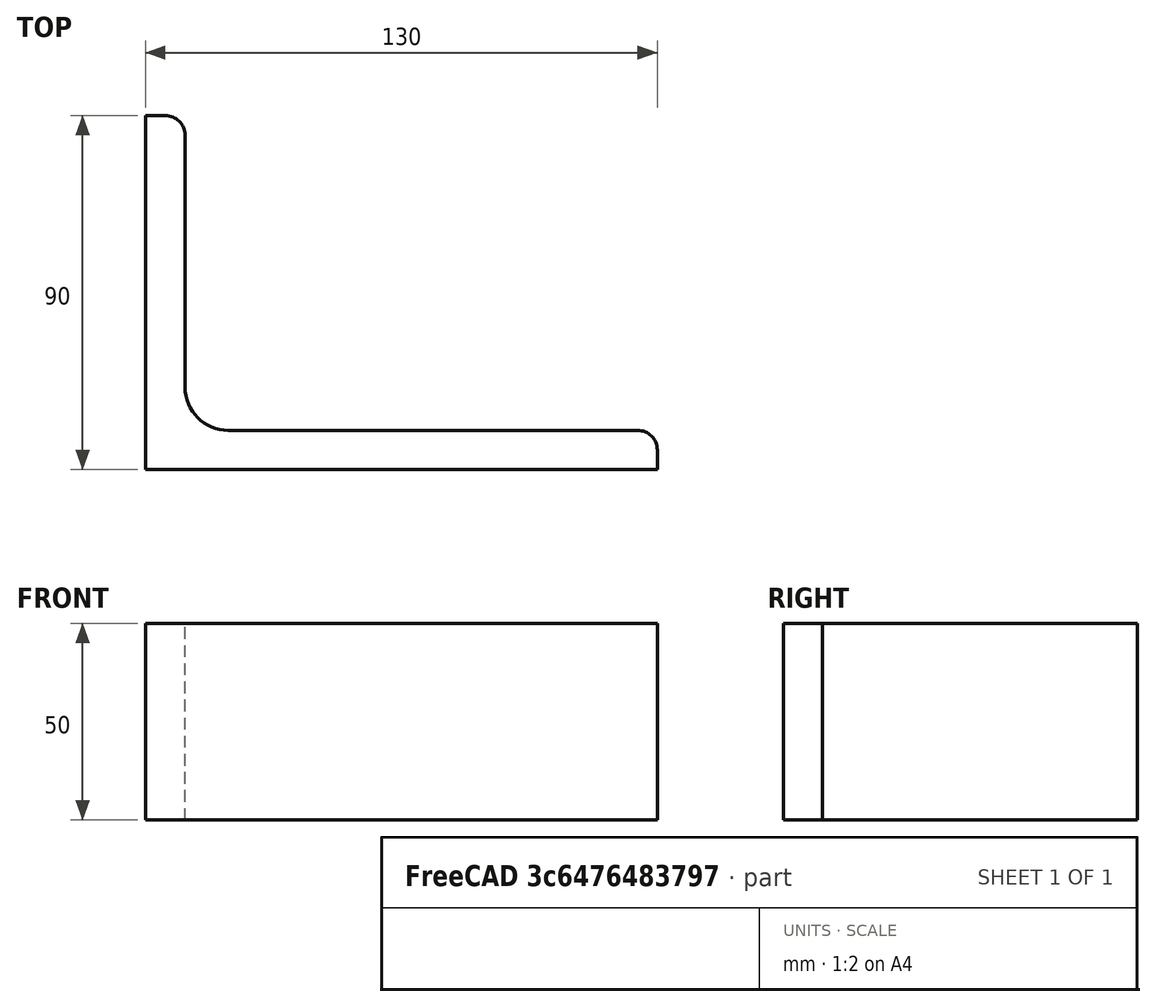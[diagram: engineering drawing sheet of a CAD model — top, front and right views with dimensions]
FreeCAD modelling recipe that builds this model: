
FCSTD DOCUMENT  (FreeCAD 0.15R4671 (Git))
Label: Angle Bar 130x90x10 EN10056 S235JR
License: All rights reserved
LicenseURL: http://en.wikipedia.org/wiki/All_rights_reserved
objects: Sketcher::SketchObject×1, Part::Extrusion×1
note: 2 computed .brp shape members not serialized (recipe doc carries the construction recipe); baked Part::Feature solids carry a one-line shape summary decoded from their .brp

FEATURE [Sketcher::SketchObject] Sketch
  sketch-geometry (9):
    g0: LineSegment StartX=0 StartY=0 StartZ=0 EndX=130 EndY=0 EndZ=0
    g1: LineSegment StartX=130 StartY=0 StartZ=0 EndX=130 EndY=5 EndZ=0
    g2: LineSegment StartX=125 StartY=10 StartZ=0 EndX=21 EndY=10 EndZ=0
    g3: LineSegment StartX=0 StartY=0 StartZ=0 EndX=0 EndY=90 EndZ=0
    g4: LineSegment StartX=0 StartY=90 StartZ=0 EndX=5 EndY=90 EndZ=0
    g5: LineSegment StartX=10 StartY=85 StartZ=0 EndX=10 EndY=21 EndZ=0
    g6: ArcOfCircle CenterX=21 CenterY=21 CenterZ=0 NormalX=0 NormalY=0 NormalZ=1 Radius=11 StartAngle=3.14159 EndAngle=4.71239
    g7: ArcOfCircle CenterX=5 CenterY=85 CenterZ=0 NormalX=0 NormalY=0 NormalZ=1 Radius=5 StartAngle=0 EndAngle=1.5708
    g8: ArcOfCircle CenterX=125 CenterY=5 CenterZ=0 NormalX=0 NormalY=0 NormalZ=1 Radius=5 StartAngle=0 EndAngle=1.5708
  constraints (23):
    c: Coincident(g0,g-1)
    c: Horizontal(g0)
    c: Coincident(g1,g0)
    c: Vertical(g1)
    c: Horizontal(g2)
    c: Coincident(g3,g-1)
    c: Vertical(g3)
    c: Coincident(g4,g3)
    c: Horizontal(g4)
    c: Vertical(g5)
    c: Tangent(g5,g6) = -1.5708
    c: Tangent(g2,g6) = 1.5708
    c: Tangent(g4,g7) = 1.5708
    c: Tangent(g5,g7) = 1.5708
    c: Tangent(g2,g8) = -1.5708
    c: Tangent(g1,g8) = -1.5708
    c: DistanceX(g0) = 130
    c: DistanceY(g3) = 90
    c: DistanceY(g0,g2) = 10
    c: DistanceX(g3,g5) = 10
    c: Radius(g6) = 11
    c: Radius(g8) = 5
    c: Radius(g7) = 5
FEATURE [Part::Extrusion] Extrude  label="Angle Bar 130x90x10 EN10056 S235JR"
  Base = -> Sketch
  Dir = (0,0,50)
  Solid = true
